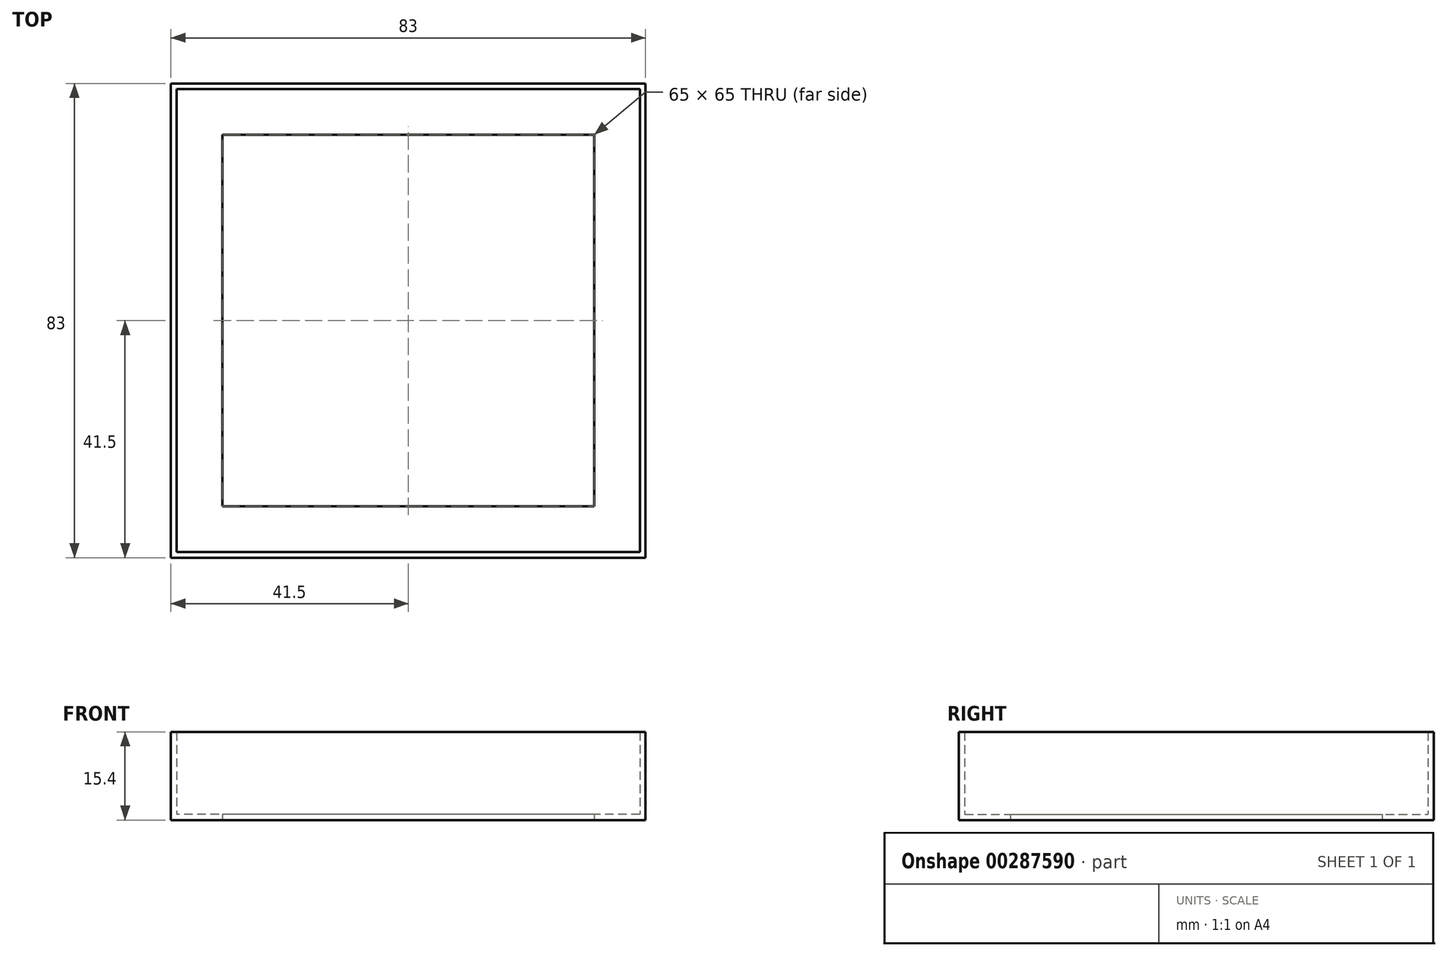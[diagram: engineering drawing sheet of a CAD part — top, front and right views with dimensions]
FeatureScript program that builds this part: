
annotation { "Feature Type Name" : "Feature", "Feature Type Description" : "" }
export const myFeature = defineFeature(function(context is Context, id is Id, definition is map)
    precondition{}
    {
        {
            var Q0;
            Q0=qCreatedBy(makeId("Top.planeOp"),FACE);
            var sketch = newSketch(context, id + "F0", { "sketchPlane" : qUnion([Q0])});
            skLineSegment(sketch, "E0.bottom", {"start": v(40.5, -40.5) * mm, "end": v(-40.5, -40.5) * mm});
            skLineSegment(sketch, "E0.top", {"start": v(40.5, 40.5) * mm, "end": v(-40.5, 40.5) * mm});
            skLineSegment(sketch, "E0.left", {"start": v(40.5, -40.5) * mm, "end": v(40.5, 40.5) * mm});
            skLineSegment(sketch, "E0.right", {"start": v(-40.5, -40.5) * mm, "end": v(-40.5, 40.5) * mm});
            skPoint(sketch, "E0.middle", {"position": v(0, 0) * mm});
            skLineSegment(sketch, "E1.bottom", {"start": v(41.5, -41.5) * mm, "end": v(-41.5, -41.5) * mm});
            skLineSegment(sketch, "E1.top", {"start": v(41.5, 41.5) * mm, "end": v(-41.5, 41.5) * mm});
            skLineSegment(sketch, "E1.left", {"start": v(41.5, -41.5) * mm, "end": v(41.5, 41.5) * mm});
            skLineSegment(sketch, "E1.right", {"start": v(-41.5, -41.5) * mm, "end": v(-41.5, 41.5) * mm});
            skLineSegment(sketch, "E2.bottom", {"start": v(32.5, -32.5) * mm, "end": v(-32.5, -32.5) * mm});
            skLineSegment(sketch, "E2.top", {"start": v(32.5, 32.5) * mm, "end": v(-32.5, 32.5) * mm});
            skLineSegment(sketch, "E2.left", {"start": v(32.5, -32.5) * mm, "end": v(32.5, 32.5) * mm});
            skLineSegment(sketch, "E2.right", {"start": v(-32.5, -32.5) * mm, "end": v(-32.5, 32.5) * mm});
            skSolve(sketch);
        }
        {
            var Q0;
            Q0=makeQuery(id+"F0.imprint","IMPRINT",FACE,{"disambiguationData":[TD([[makeQuery(id+"F0.imprint","IMPRINT",EDGE,{"derivedFrom":sQuery(id+"F0.wireOp",EDGE,"E0.bottom")}),-1.0]])]});
            extrude(context, id + "F1", {"entities" : qUnion([Q0]), "depth" : 1 * mm, "offsetDistance" : 25 * mm});
        }
        {
            var Q0;
            Q0=makeQuery(id+"F0.imprint","IMPRINT",FACE,{"disambiguationData":[TD([[makeQuery(id+"F0.imprint","IMPRINT",EDGE,{"derivedFrom":sQuery(id+"F0.wireOp",EDGE,"E0.bottom")}),1.0]])]});
            extrude(context, id + "F2", {"entities" : qUnion([Q0]), "operationType" : NewBodyOperationType.ADD, "depth" : 15.4 * mm, "offsetDistance" : 25 * mm});
        }
    });
